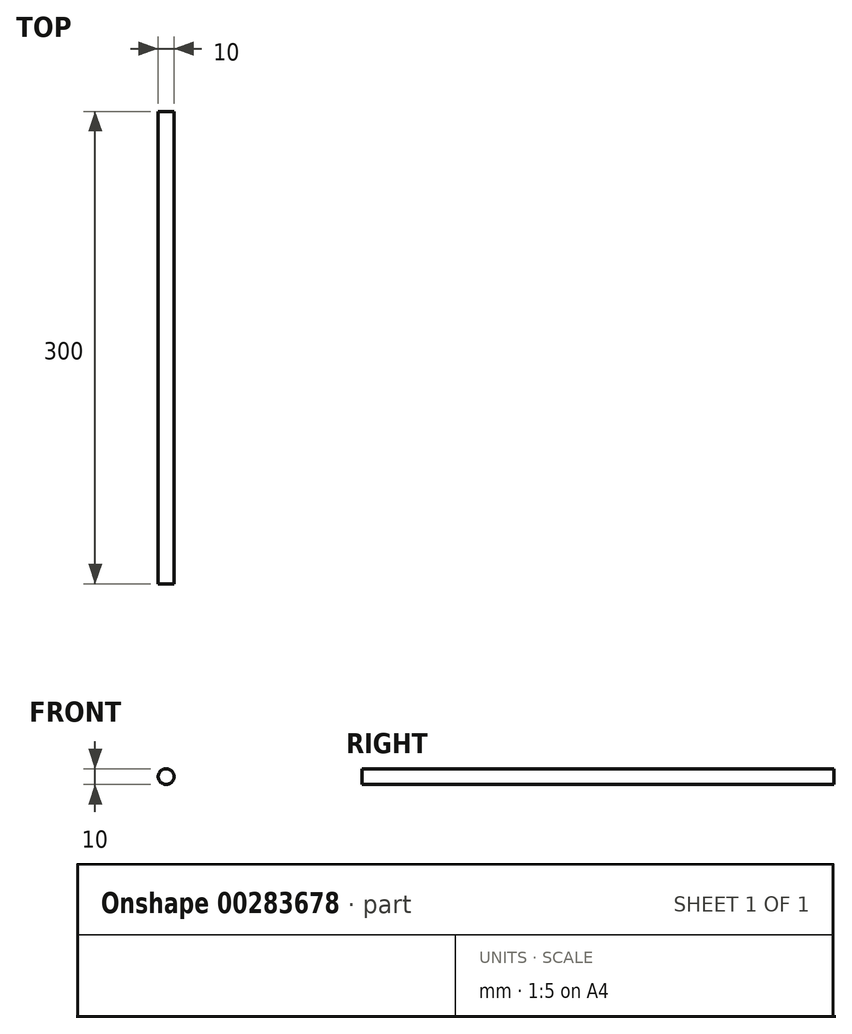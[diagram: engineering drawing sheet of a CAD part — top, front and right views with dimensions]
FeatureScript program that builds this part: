
annotation { "Feature Type Name" : "Feature", "Feature Type Description" : "" }
export const myFeature = defineFeature(function(context is Context, id is Id, definition is map)
    precondition{}
    {
        {
            var Q0;
            Q0=qCreatedBy(makeId("Front.planeOp"),FACE);
            var sketch = newSketch(context, id + "F0", { "sketchPlane" : qUnion([Q0])});
            skCircle(sketch, "E0", {"center": v(0, 0) * mm, "radius": 5 * mm});
            skSolve(sketch);
        }
        {
            var Q0;
            Q0=makeQuery(id+"F0.imprint","IMPRINT",FACE,{"disambiguationData":[TD([[makeQuery(id+"F0.imprint","IMPRINT",EDGE,{"derivedFrom":sQuery(id+"F0.wireOp",EDGE,"E0")}),1.0]])]});
            var Q1;
            Q1=sQuery(id+"F0.wireOp",EDGE,"E0");
            extrude(context, id + "F1", {"entities" : qUnion([Q0]), "surfaceEntities" : qUnion([Q1]), "endBound" : BoundingType.SYMMETRIC, "depth" : 300 * mm});
        }
    });
